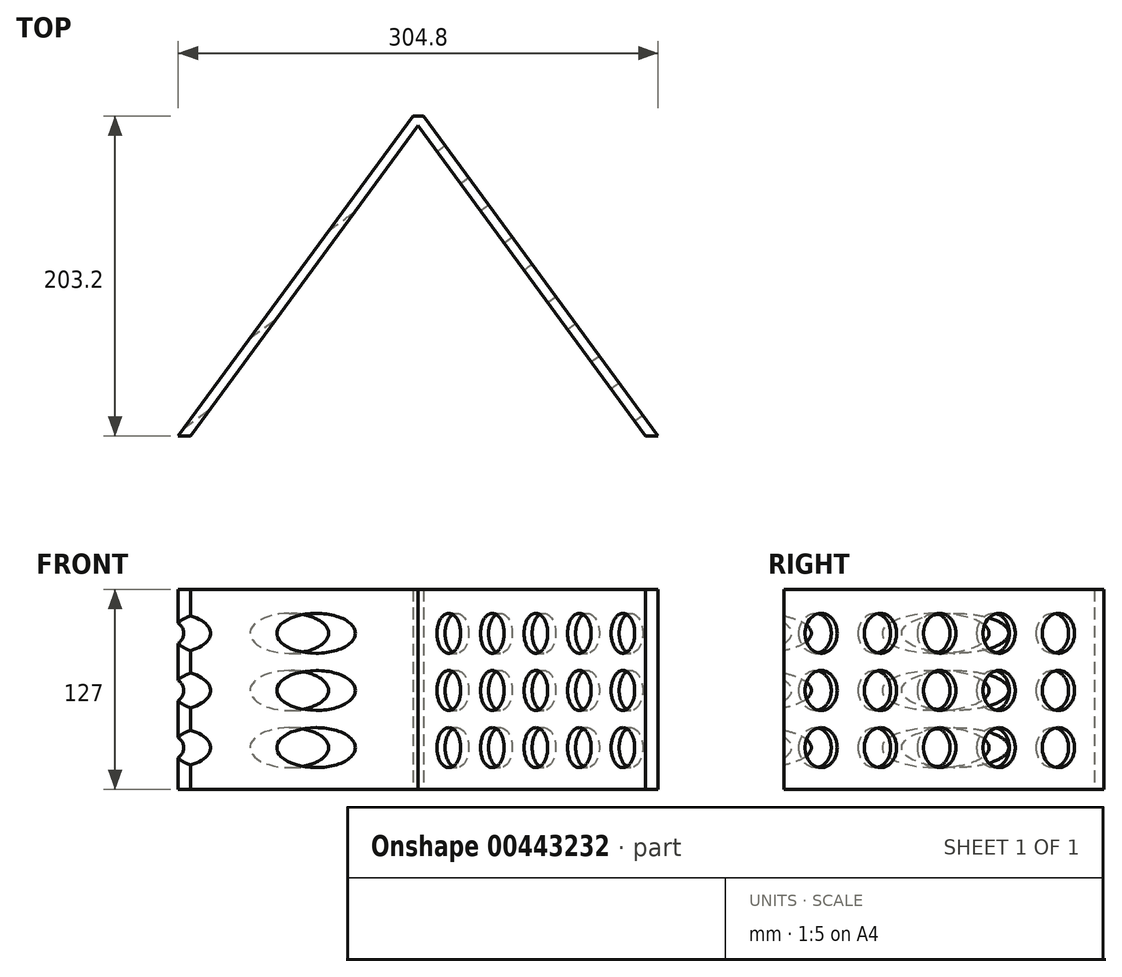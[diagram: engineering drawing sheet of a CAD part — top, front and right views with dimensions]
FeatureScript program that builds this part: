
annotation { "Feature Type Name" : "Feature", "Feature Type Description" : "" }
export const myFeature = defineFeature(function(context is Context, id is Id, definition is map)
    precondition{}
    {
        {
            var Q0;
            Q0=qCreatedBy(makeId("Top.planeOp"),FACE);
            var sketch = newSketch(context, id + "F0", { "sketchPlane" : qUnion([Q0])});
            skLineSegment(sketch, "E0.bottom", {"start": v(-152.4, 101.6) * mm, "end": v(152.4, 101.6) * mm, "construction": true});
            skLineSegment(sketch, "E0.top", {"start": v(-152.4, -101.6) * mm, "end": v(152.4, -101.6) * mm, "construction": true});
            skLineSegment(sketch, "E0.left", {"start": v(-152.4, 101.6) * mm, "end": v(-152.4, -101.6) * mm, "construction": true});
            skLineSegment(sketch, "E0.right", {"start": v(152.4, 101.6) * mm, "end": v(152.4, -101.6) * mm, "construction": true});
            skPoint(sketch, "E0.middle", {"position": v(0, 0) * mm});
            skLineSegment(sketch, "E1", {"start": v(0, 101.6) * mm, "end": v(0, -101.6) * mm, "construction": true});
            skLineSegment(sketch, "E2", {"start": v(3.37, 101.6) * mm, "end": v(152.4, -101.6) * mm});
            skLineSegment(sketch, "E3", {"start": v(144.53, -101.6) * mm, "end": v(0, 95.46) * mm});
            skLineSegment(sketch, "E4", {"start": v(144.53, -101.6) * mm, "end": v(152.4, -101.6) * mm});
            skLineSegment(sketch, "E5", {"start": v(3.37, 101.6) * mm, "end": v(0, 101.6) * mm});
            skLineSegment(sketch, "E6.MirrorCS", {"start": v(-3.37, 101.6) * mm, "end": v(0, 101.6) * mm});
            skLineSegment(sketch, "E7.MirrorCS", {"start": v(-144.53, -101.6) * mm, "end": v(0, 95.46) * mm});
            skLineSegment(sketch, "E8", {"start": v(-3.37, 101.6) * mm, "end": v(-152.4, -101.6) * mm});
            skLineSegment(sketch, "E9", {"start": v(-152.4, -101.6) * mm, "end": v(-144.53, -101.6) * mm});
            skSolve(sketch);
        }
        {
            var Q0;
            Q0 = qSketchRegion(id + "F0", true);
            extrude(context, id + "F1", {"entities" : qUnion([Q0]), "depth" : 127 * mm});
        }
        {
            var Q0;
            Q0=makeQuery(id+"F1.opExtrude","SWEPT_FACE",FACE,{"disambiguationData":[OSD([sQuery(id+"F0.wireOp",EDGE,"E2")])]});
            var sketch = newSketch(context, id + "F2", { "sketchPlane" : qUnion([Q0])});
            skCircle(sketch, "E10", {"center": v(-142.9, 99.18) * mm, "radius": 12.7 * mm});
            skCircle(sketch, "E11.0.1.0", {"center": v(-142.9, 62.86) * mm, "radius": 12.7 * mm});
            skCircle(sketch, "E11.0.2.0", {"center": v(-142.9, 26.54) * mm, "radius": 12.7 * mm});
            skCircle(sketch, "E11.1.0.0", {"center": v(-96.17, 99.18) * mm, "radius": 12.7 * mm});
            skCircle(sketch, "E11.1.1.0", {"center": v(-96.17, 62.86) * mm, "radius": 12.7 * mm});
            skCircle(sketch, "E11.1.2.0", {"center": v(-96.17, 26.54) * mm, "radius": 12.7 * mm});
            skCircle(sketch, "E11.2.0.0", {"center": v(-49.43, 99.18) * mm, "radius": 12.7 * mm});
            skCircle(sketch, "E11.2.1.0", {"center": v(-49.43, 62.86) * mm, "radius": 12.7 * mm});
            skCircle(sketch, "E11.2.2.0", {"center": v(-49.43, 26.54) * mm, "radius": 12.7 * mm});
            skCircle(sketch, "E11.3.0.0", {"center": v(-2.7, 99.18) * mm, "radius": 12.7 * mm});
            skCircle(sketch, "E11.3.1.0", {"center": v(-2.7, 62.86) * mm, "radius": 12.7 * mm});
            skCircle(sketch, "E11.3.2.0", {"center": v(-2.7, 26.54) * mm, "radius": 12.7 * mm});
            skCircle(sketch, "E11.4.0.0", {"center": v(44.04, 99.18) * mm, "radius": 12.7 * mm});
            skCircle(sketch, "E11.4.1.0", {"center": v(44.04, 62.86) * mm, "radius": 12.7 * mm});
            skCircle(sketch, "E11.4.2.0", {"center": v(44.04, 26.54) * mm, "radius": 12.7 * mm});
            skLineSegment(sketch, "E11.direction1", {"start": v(-142.9, 99.18) * mm, "end": v(-96.17, 99.18) * mm, "construction": true});
            skLineSegment(sketch, "E11.direction2", {"start": v(-142.9, 99.18) * mm, "end": v(-142.9, 62.86) * mm, "construction": true});
            skSolve(sketch);
        }
        {
            var Q0;
            Q0 = qSketchRegion(id + "F2", true);
            extrude(context, id + "F3", {"entities" : qUnion([Q0]), "operationType" : NewBodyOperationType.REMOVE, "endBound" : BoundingType.THROUGH_ALL, "oppositeDirection" : true, "depth" : 25.4 * mm});
        }
    });
